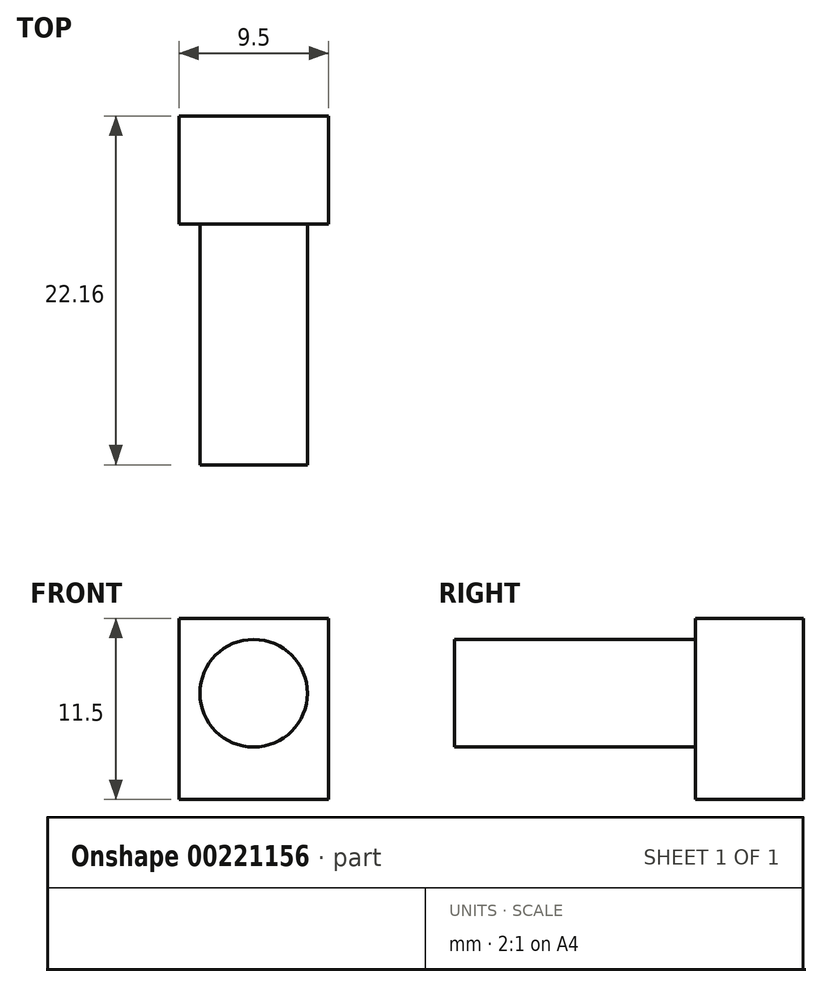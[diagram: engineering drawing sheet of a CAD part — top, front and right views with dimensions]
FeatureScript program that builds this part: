
annotation { "Feature Type Name" : "Feature", "Feature Type Description" : "" }
export const myFeature = defineFeature(function(context is Context, id is Id, definition is map)
    precondition{}
    {
        {
            var Q0;
            Q0=qCreatedBy(makeId("Top.planeOp"),FACE);
            var sketch = newSketch(context, id + "F0", { "sketchPlane" : qUnion([Q0])});
            skLineSegment(sketch, "E0.bottom", {"start": v(-11.82, 10.92) * mm, "end": v(-2.32, 10.92) * mm});
            skLineSegment(sketch, "E0.top", {"start": v(-11.82, 4.07) * mm, "end": v(-2.32, 4.07) * mm});
            skLineSegment(sketch, "E0.left", {"start": v(-11.82, 10.92) * mm, "end": v(-11.82, 4.07) * mm});
            skLineSegment(sketch, "E0.right", {"start": v(-2.32, 10.92) * mm, "end": v(-2.32, 4.07) * mm});
            skSolve(sketch);
        }
        {
            var Q0;
            Q0=makeQuery(id+"F0.imprint","IMPRINT",FACE,{"disambiguationData":[TD([[makeQuery(id+"F0.imprint","IMPRINT",EDGE,{"derivedFrom":sQuery(id+"F0.wireOp",EDGE,"E0.bottom")}),-1.0]])]});
            extrude(context, id + "F1", {"entities" : qUnion([Q0]), "depth" : 11.5 * mm});
        }
        {
            var Q0;
            Q0=makeQuery(id+"F1.opExtrude","SWEPT_FACE",FACE,{"disambiguationData":[OSD([sQuery(id+"F0.wireOp",EDGE,"E0.bottom")])]});
            var sketch = newSketch(context, id + "F2", { "sketchPlane" : qUnion([Q0])});
            skCircle(sketch, "E1", {"center": v(7.07, 6.75) * mm, "radius": 3.42 * mm});
            skLineSegment(sketch, "E2", {"start": v(10.48, 6.75) * mm, "end": v(11.82, 6.75) * mm, "construction": true});
            skLineSegment(sketch, "E3", {"start": v(7.07, 11.5) * mm, "end": v(7.07, 10.17) * mm, "construction": true});
            skSolve(sketch);
        }
        {
            var Q0;
            Q0=makeQuery(id+"F2.imprint","IMPRINT",FACE,{"disambiguationData":[TD([[makeQuery(id+"F2.imprint","IMPRINT",EDGE,{"derivedFrom":sQuery(id+"F2.wireOp",EDGE,"E1")}),1.0]])]});
            var Q1;
            Q1=sQuery(id+"F2.wireOp",EDGE,"E1");
            extrude(context, id + "F3", {"entities" : qUnion([Q0]), "operationType" : NewBodyOperationType.ADD, "surfaceEntities" : qUnion([Q1]), "oppositeDirection" : true, "depth" : 22.16 * mm});
        }
    });
